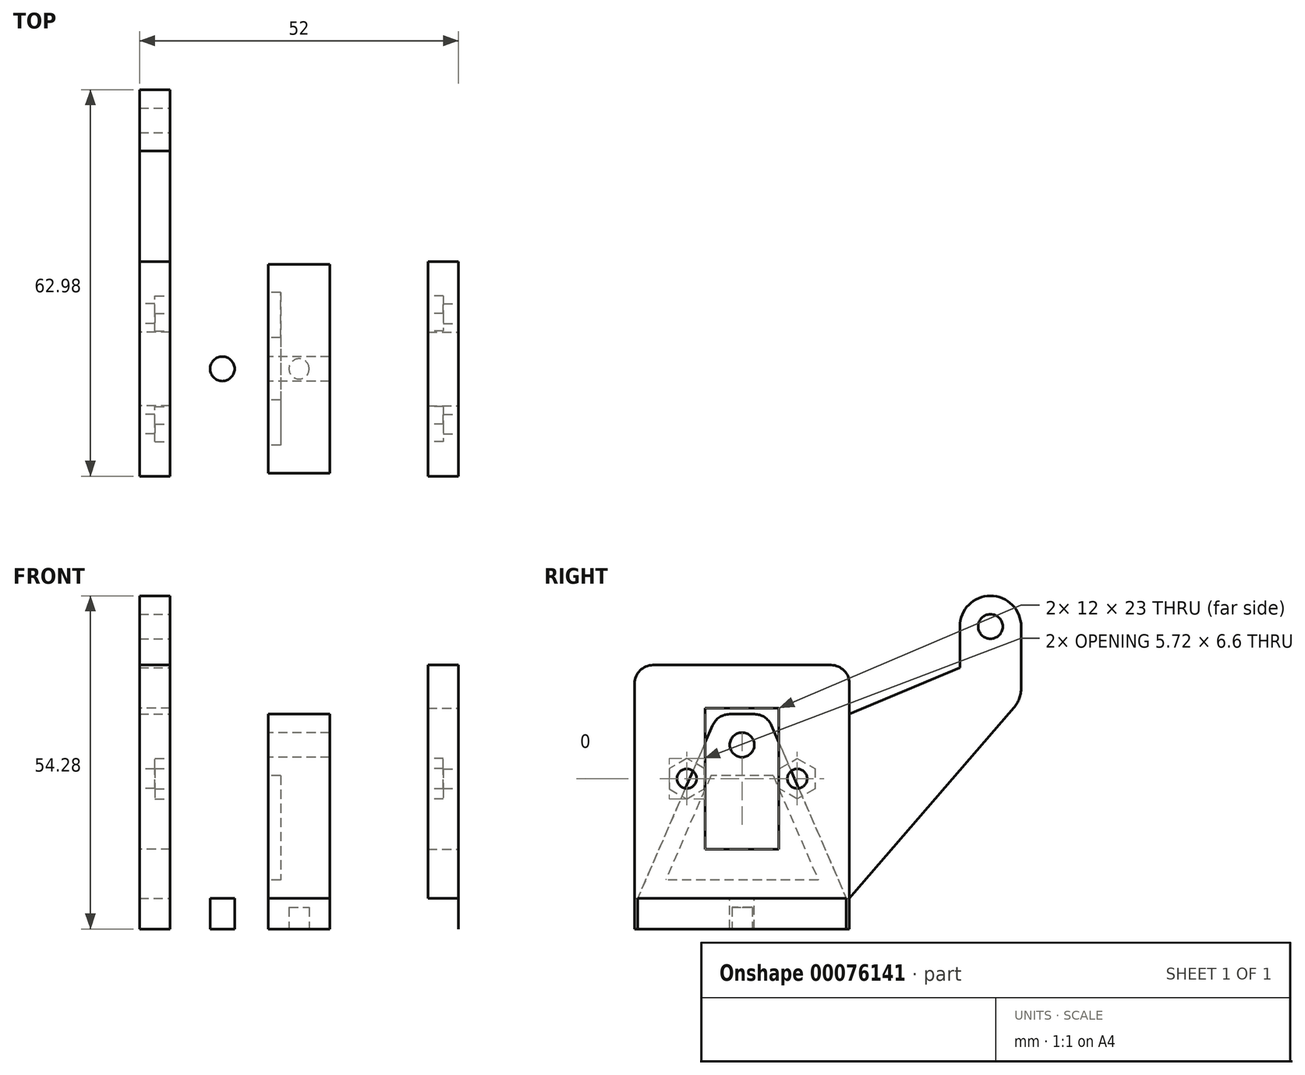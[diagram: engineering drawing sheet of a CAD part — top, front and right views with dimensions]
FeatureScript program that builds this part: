
annotation { "Feature Type Name" : "Feature", "Feature Type Description" : "" }
export const myFeature = defineFeature(function(context is Context, id is Id, definition is map)
    precondition{}
    {
        {
            var Q0;
            Q0=qCreatedBy(makeId("Top.planeOp"),FACE);
            var sketch = newSketch(context, id + "F0", { "sketchPlane" : qUnion([Q0])});
            skLineSegment(sketch, "E0.bottom", {"start": v(-23, 20) * mm, "end": v(23, 20) * mm});
            skLineSegment(sketch, "E0.top", {"start": v(-23, -20) * mm, "end": v(23, -20) * mm});
            skLineSegment(sketch, "E0.left", {"start": v(-26, 17) * mm, "end": v(-26, -17) * mm});
            skLineSegment(sketch, "E0.right", {"start": v(26, 17) * mm, "end": v(26, -17) * mm});
            skPoint(sketch, "E0.middle", {"position": v(0, 0) * mm});
            skPoint(sketch, "E1.visualSharp", {"position": v(-26, 20) * mm});
            skArc(sketch, "E1.filletArc", {"start": v(-23, 20) * mm, "mid": v(-25.12, 19.12) * mm, "end": v(-26, 17) * mm});
            skPoint(sketch, "E2.visualSharp", {"position": v(-26, -20) * mm});
            skArc(sketch, "E2.filletArc", {"start": v(-26, -17) * mm, "mid": v(-25.12, -19.12) * mm, "end": v(-23, -20) * mm});
            skPoint(sketch, "E3.visualSharp", {"position": v(26, -20) * mm});
            skArc(sketch, "E3.filletArc", {"start": v(23, -20) * mm, "mid": v(25.12, -19.12) * mm, "end": v(26, -17) * mm});
            skPoint(sketch, "E4.visualSharp", {"position": v(26, 20) * mm});
            skArc(sketch, "E4.filletArc", {"start": v(26, 17) * mm, "mid": v(25.12, 19.12) * mm, "end": v(23, 20) * mm});
            skSolve(sketch);
        }
        {
            var Q0;
            Q0 = qSketchRegion(id + "F0", true);
            extrude(context, id + "F1", {"entities" : qUnion([Q0]), "depth" : 5 * mm});
        }
        {
            var Q0;
            Q0=makeQuery(id+"F1.opExtrude","CAP_FACE",FACE,{"disambiguationData":[OSD([sQuery(id+"F0.wireOp",EDGE,"E0.bottom"),sQuery(id+"F0.wireOp",EDGE,"E0.top"),sQuery(id+"F0.wireOp",EDGE,"E0.left"),sQuery(id+"F0.wireOp",EDGE,"E0.right"),sQuery(id+"F0.wireOp",EDGE,"E1.filletArc"),sQuery(id+"F0.wireOp",EDGE,"E2.filletArc"),sQuery(id+"F0.wireOp",EDGE,"E3.filletArc"),sQuery(id+"F0.wireOp",EDGE,"E4.filletArc")])],"isStart":true});
            var sketch = newSketch(context, id + "F2", { "sketchPlane" : qUnion([Q0])});
            skCircle(sketch, "E5", {"center": v(0, 0) * mm, "radius": 1.65 * mm});
            skSolve(sketch);
        }
        {
            var Q0;
            Q0 = qSketchRegion(id + "F2", true);
            extrude(context, id + "F3", {"entities" : qUnion([Q0]), "operationType" : NewBodyOperationType.REMOVE, "oppositeDirection" : true, "depth" : 3.5 * mm});
        }
        {
            var Q0;
            Q0=qCreatedBy(makeId("Right.planeOp"),FACE);
            var sketch = newSketch(context, id + "F4", { "sketchPlane" : qUnion([Q0])});
            skLineSegment(sketch, "E6.0", {"start": v(17, 5) * mm, "end": v(-17, 5) * mm});
            skLineSegment(sketch, "E7", {"start": v(0, 5) * mm, "end": v(0, 35) * mm});
            skPoint(sketch, "E7.endSnap0", {"position": v(0, 5) * mm});
            skLineSegment(sketch, "E8", {"start": v(2.03, 35) * mm, "end": v(-2.03, 35) * mm});
            skLineSegment(sketch, "E9", {"start": v(4.78, 33.2) * mm, "end": v(17, 5) * mm});
            skLineSegment(sketch, "E10", {"start": v(-4.78, 33.2) * mm, "end": v(-17, 5) * mm});
            skPoint(sketch, "E11.visualSharp", {"position": v(4, 35) * mm});
            skArc(sketch, "E11.filletArc", {"start": v(4.78, 33.2) * mm, "mid": v(3.68, 34.5) * mm, "end": v(2.03, 35) * mm});
            skPoint(sketch, "E12.visualSharp", {"position": v(-4, 35) * mm});
            skArc(sketch, "E12.filletArc", {"start": v(-2.03, 35) * mm, "mid": v(-3.68, 34.5) * mm, "end": v(-4.78, 33.2) * mm});
            skSolve(sketch);
        }
        {
            var Q0;
            Q0 = qSketchRegion(id + "F4", true);
            extrude(context, id + "F5", {"entities" : qUnion([Q0]), "operationType" : NewBodyOperationType.ADD, "depth" : 5 * mm, "hasSecondDirection" : true, "secondDirectionOppositeDirection" : true, "secondDirectionDepth" : 5 * mm});
        }
        {
            var Q0;
            Q0=makeQuery(id+"F1.opExtrude","SWEPT_FACE",FACE,{"disambiguationData":[OSD([sQuery(id+"F0.wireOp",EDGE,"E0.right")])]});
            var sketch = newSketch(context, id + "F6", { "sketchPlane" : qUnion([Q0])});
            skLineSegment(sketch, "E13.bottom", {"start": v(17.5, 0) * mm, "end": v(-17.5, 0) * mm});
            skLineSegment(sketch, "E13.top", {"start": v(14.5, 43) * mm, "end": v(-14.5, 43) * mm});
            skLineSegment(sketch, "E13.left", {"start": v(17.5, 0) * mm, "end": v(17.5, 40) * mm});
            skLineSegment(sketch, "E13.right", {"start": v(-17.5, 0) * mm, "end": v(-17.5, 40) * mm});
            skLineSegment(sketch, "E14", {"start": v(0, 0) * mm, "end": v(0, 49) * mm, "construction": true});
            skPoint(sketch, "E15.visualSharp", {"position": v(17.5, 43) * mm});
            skArc(sketch, "E15.filletArc", {"start": v(17.5, 40) * mm, "mid": v(16.62, 42.12) * mm, "end": v(14.5, 43) * mm});
            skPoint(sketch, "E16.visualSharp", {"position": v(-17.5, 43) * mm});
            skArc(sketch, "E16.filletArc", {"start": v(-14.5, 43) * mm, "mid": v(-16.62, 42.12) * mm, "end": v(-17.5, 40) * mm});
            skLineSegment(sketch, "E17.bottom", {"start": v(6, 36) * mm, "end": v(-6, 36) * mm});
            skLineSegment(sketch, "E17.top", {"start": v(6, 13) * mm, "end": v(-6, 13) * mm});
            skLineSegment(sketch, "E17.left", {"start": v(6, 36) * mm, "end": v(6, 13) * mm});
            skLineSegment(sketch, "E17.right", {"start": v(-6, 36) * mm, "end": v(-6, 13) * mm});
            skPoint(sketch, "E17.middle", {"position": v(0, 24.5) * mm});
            skLineSegment(sketch, "E18", {"start": v(-17.5, 24.5) * mm, "end": v(17.5, 24.5) * mm, "construction": true});
            skCircle(sketch, "E19", {"center": v(-9, 24.5) * mm, "radius": 1.6 * mm});
            skCircle(sketch, "E20.MirrorC", {"center": v(9, 24.5) * mm, "radius": 1.6 * mm});
            skSolve(sketch);
        }
        {
            var Q0;
            Q0=makeQuery(id+"F6.imprint","IMPRINT",FACE,{"disambiguationData":[TD([[makeQuery(id+"F6.imprint","IMPRINT",EDGE,{"derivedFrom":sQuery(id+"F6.wireOp",EDGE,"E13.top")}),1.0]])]});
            extrude(context, id + "F7", {"entities" : qUnion([Q0]), "oppositeDirection" : true, "depth" : 5 * mm});
        }
        {
            var Q0;
            Q0=makeQuery(id+"F7.opExtrude","CAP_FACE",FACE,{"disambiguationData":[OSD([sQuery(id+"F0.wireOp",EDGE,"E0.right"),sQuery(id+"F0.wireOp",EDGE,"E3.filletArc"),sQuery(id+"F0.wireOp",EDGE,"E4.filletArc"),sQuery(id+"F6.wireOp",EDGE,"E13.bottom"),sQuery(id+"F6.wireOp",EDGE,"E13.top"),sQuery(id+"F6.wireOp",EDGE,"E13.left"),sQuery(id+"F6.wireOp",EDGE,"E13.right"),sQuery(id+"F6.wireOp",EDGE,"E15.filletArc"),sQuery(id+"F6.wireOp",EDGE,"E16.filletArc"),sQuery(id+"F6.wireOp",EDGE,"E17.bottom"),sQuery(id+"F6.wireOp",EDGE,"E17.top"),sQuery(id+"F6.wireOp",EDGE,"E17.left"),sQuery(id+"F6.wireOp",EDGE,"E17.right"),sQuery(id+"F6.wireOp",EDGE,"E19"),sQuery(id+"F6.wireOp",EDGE,"E20.MirrorC")])],"isStart":false});
            var sketch = newSketch(context, id + "F8", { "sketchPlane" : qUnion([Q0])});
            skLineSegment(sketch, "E21", {"start": v(0, 5) * mm, "end": v(0, 43) * mm, "construction": true});
            skCircle(sketch, "E22.cCircle", {"center": v(9, 24.5) * mm, "radius": 2.86 * mm, "construction": true});
            skLineSegment(sketch, "E22.0", {"start": v(9, 27.8) * mm, "end": v(11.86, 26.15) * mm});
            skLineSegment(sketch, "E22.1", {"start": v(11.86, 26.15) * mm, "end": v(11.86, 22.85) * mm});
            skLineSegment(sketch, "E22.2", {"start": v(11.86, 22.85) * mm, "end": v(9, 21.2) * mm});
            skLineSegment(sketch, "E22.3", {"start": v(9, 21.2) * mm, "end": v(6.14, 22.85) * mm});
            skLineSegment(sketch, "E22.4", {"start": v(6.14, 22.85) * mm, "end": v(6.14, 26.15) * mm});
            skLineSegment(sketch, "E22.5", {"start": v(6.14, 26.15) * mm, "end": v(9, 27.8) * mm});
            skPoint(sketch, "E22.0.midPoint", {"position": v(10.43, 26.98) * mm});
            skLineSegment(sketch, "E23.MirrorCS", {"start": v(-9, 21.2) * mm, "end": v(-6.14, 22.85) * mm});
            skLineSegment(sketch, "E24.MirrorCS", {"start": v(-6.14, 22.85) * mm, "end": v(-6.14, 26.15) * mm});
            skCircle(sketch, "E25.MirrorC", {"center": v(-9, 24.5) * mm, "radius": 2.86 * mm, "construction": true});
            skLineSegment(sketch, "E26.MirrorCS", {"start": v(-6.14, 26.15) * mm, "end": v(-9, 27.8) * mm});
            skLineSegment(sketch, "E27.MirrorCS", {"start": v(-9, 27.8) * mm, "end": v(-11.86, 26.15) * mm});
            skLineSegment(sketch, "E28.MirrorCS", {"start": v(-11.86, 22.85) * mm, "end": v(-9, 21.2) * mm});
            skLineSegment(sketch, "E29.MirrorCS", {"start": v(-11.86, 26.15) * mm, "end": v(-11.86, 22.85) * mm});
            skSolve(sketch);
        }
        {
            var Q0;
            Q0 = qSketchRegion(id + "F8", true);
            extrude(context, id + "F9", {"entities" : qUnion([Q0]), "operationType" : NewBodyOperationType.REMOVE, "oppositeDirection" : true, "depth" : 2.5 * mm});
        }
        {
            var Q0;
            Q0=makeQuery(id+"F7.opExtrude","SWEPT_BODY",BODY,{"disambiguationData":[OSD([sQuery(id+"F0.wireOp",EDGE,"E0.right"),sQuery(id+"F0.wireOp",EDGE,"E3.filletArc"),sQuery(id+"F0.wireOp",EDGE,"E4.filletArc"),sQuery(id+"F6.wireOp",EDGE,"E13.bottom"),sQuery(id+"F6.wireOp",EDGE,"E13.top"),sQuery(id+"F6.wireOp",EDGE,"E13.left"),sQuery(id+"F6.wireOp",EDGE,"E13.right"),sQuery(id+"F6.wireOp",EDGE,"E15.filletArc"),sQuery(id+"F6.wireOp",EDGE,"E16.filletArc")])]});
            transform(context, id + "F10", {"entities" : qUnion([Q0]), "transformType" : TransformType.TRANSLATION_3D, "dx" : -47 * mm, "dy" : 0 * mm, "dz" : 0 * mm, "makeCopy" : true});
        }
        {
            var Q0;
            Q0=makeQuery(id+"F10.opPattern","COPY",FACE,{"derivedFrom":makeQuery(id+"F7.opExtrude","CAP_FACE",FACE,{"disambiguationData":[OSD([sQuery(id+"F0.wireOp",EDGE,"E0.right"),sQuery(id+"F0.wireOp",EDGE,"E3.filletArc"),sQuery(id+"F0.wireOp",EDGE,"E4.filletArc"),sQuery(id+"F6.wireOp",EDGE,"E13.bottom"),sQuery(id+"F6.wireOp",EDGE,"E13.top"),sQuery(id+"F6.wireOp",EDGE,"E13.left"),sQuery(id+"F6.wireOp",EDGE,"E13.right"),sQuery(id+"F6.wireOp",EDGE,"E15.filletArc"),sQuery(id+"F6.wireOp",EDGE,"E16.filletArc"),sQuery(id+"F6.wireOp",EDGE,"E17.bottom"),sQuery(id+"F6.wireOp",EDGE,"E17.top"),sQuery(id+"F6.wireOp",EDGE,"E17.left"),sQuery(id+"F6.wireOp",EDGE,"E17.right"),sQuery(id+"F6.wireOp",EDGE,"E19"),sQuery(id+"F6.wireOp",EDGE,"E20.MirrorC")])],"isStart":false}),"instanceName":"1"});
            var Q1;
            Q1=makeQuery(id+"F10.opPattern","COPY",FACE,{"derivedFrom":makeQuery(id+"F7.opExtrude","CAP_FACE",FACE,{"disambiguationData":[OSD([sQuery(id+"F0.wireOp",EDGE,"E0.right"),sQuery(id+"F0.wireOp",EDGE,"E3.filletArc"),sQuery(id+"F0.wireOp",EDGE,"E4.filletArc"),sQuery(id+"F6.wireOp",EDGE,"E13.bottom"),sQuery(id+"F6.wireOp",EDGE,"E13.top"),sQuery(id+"F6.wireOp",EDGE,"E13.left"),sQuery(id+"F6.wireOp",EDGE,"E13.right"),sQuery(id+"F6.wireOp",EDGE,"E15.filletArc"),sQuery(id+"F6.wireOp",EDGE,"E16.filletArc"),sQuery(id+"F6.wireOp",EDGE,"E17.bottom"),sQuery(id+"F6.wireOp",EDGE,"E17.top"),sQuery(id+"F6.wireOp",EDGE,"E17.left"),sQuery(id+"F6.wireOp",EDGE,"E17.right"),sQuery(id+"F6.wireOp",EDGE,"E19"),sQuery(id+"F6.wireOp",EDGE,"E20.MirrorC")])],"isStart":true}),"instanceName":"1"});
            cPlane(context, id + "F11", {"entities" : qUnion([Q0, Q1]), "cplaneType" : CPlaneType.MID_PLANE, "offset" : 150 * mm, "width" : 150 * mm, "height" : 150 * mm});
        }
        {
            var Q0;
            Q0=qCreatedBy(id+"F11.planeOp",FACE);
            var sketch = newSketch(context, id + "F12", { "sketchPlane" : qUnion([Q0])});
            skLineSegment(sketch, "E30", {"start": v(0, 0) * mm, "end": v(0, 42.9) * mm, "construction": true});
            skSolve(sketch);
        }
        {
            var Q0;
            Q0=makeQuery(id+"F10.opPattern","COPY",BODY,{"derivedFrom":makeQuery(id+"F7.opExtrude","SWEPT_BODY",BODY,{"disambiguationData":[OSD([sQuery(id+"F0.wireOp",EDGE,"E0.right"),sQuery(id+"F0.wireOp",EDGE,"E3.filletArc"),sQuery(id+"F0.wireOp",EDGE,"E4.filletArc"),sQuery(id+"F6.wireOp",EDGE,"E13.bottom"),sQuery(id+"F6.wireOp",EDGE,"E13.top"),sQuery(id+"F6.wireOp",EDGE,"E13.left"),sQuery(id+"F6.wireOp",EDGE,"E13.right"),sQuery(id+"F6.wireOp",EDGE,"E15.filletArc"),sQuery(id+"F6.wireOp",EDGE,"E16.filletArc"),sQuery(id+"F6.wireOp",EDGE,"E17.bottom"),sQuery(id+"F6.wireOp",EDGE,"E17.top"),sQuery(id+"F6.wireOp",EDGE,"E17.left"),sQuery(id+"F6.wireOp",EDGE,"E17.right"),sQuery(id+"F6.wireOp",EDGE,"E19"),sQuery(id+"F6.wireOp",EDGE,"E20.MirrorC")])]}),"instanceName":"1"});
            var Q1;
            Q1=sQuery(id+"F12.wireOp",EDGE,"E30");
            transform(context, id + "F13", {"entities" : qUnion([Q0]), "transformType" : TransformType.ROTATION, "transformAxis" : qUnion([Q1]), "angle" : 180 * degree, "makeCopy" : false});
        }
        {
            var Q0;
            Q0=makeQuery(id+"F5.opExtrude","CAP_FACE",FACE,{"disambiguationData":[OSD([sQuery(id+"F4.wireOp",EDGE,"E6.0"),sQuery(id+"F4.wireOp",EDGE,"E8"),sQuery(id+"F4.wireOp",EDGE,"E9"),sQuery(id+"F4.wireOp",EDGE,"E10"),sQuery(id+"F4.wireOp",EDGE,"E11.filletArc"),sQuery(id+"F4.wireOp",EDGE,"E12.filletArc")])],"isStart":true});
            var sketch = newSketch(context, id + "F14", { "sketchPlane" : qUnion([Q0])});
            skCircle(sketch, "E31", {"center": v(0, 30) * mm, "radius": 2 * mm});
            skSolve(sketch);
        }
        {
            var Q0;
            Q0=makeQuery(id+"F14.imprint","IMPRINT",FACE,{"disambiguationData":[TD([[makeQuery(id+"F14.imprint","IMPRINT",EDGE,{"derivedFrom":sQuery(id+"F14.wireOp",EDGE,"E31")}),1.0]])]});
            extrude(context, id + "F15", {"entities" : qUnion([Q0]), "operationType" : NewBodyOperationType.REMOVE, "oppositeDirection" : true, "depth" : 25 * mm});
        }
        {
            var Q0;
            Q0=makeQuery(id+"F10.opPattern","COPY",FACE,{"derivedFrom":makeQuery(id+"F7.opExtrude","CAP_FACE",FACE,{"disambiguationData":[OSD([sQuery(id+"F0.wireOp",EDGE,"E0.right"),sQuery(id+"F0.wireOp",EDGE,"E3.filletArc"),sQuery(id+"F0.wireOp",EDGE,"E4.filletArc"),sQuery(id+"F6.wireOp",EDGE,"E13.bottom"),sQuery(id+"F6.wireOp",EDGE,"E13.top"),sQuery(id+"F6.wireOp",EDGE,"E13.left"),sQuery(id+"F6.wireOp",EDGE,"E13.right"),sQuery(id+"F6.wireOp",EDGE,"E15.filletArc"),sQuery(id+"F6.wireOp",EDGE,"E16.filletArc"),sQuery(id+"F6.wireOp",EDGE,"E17.bottom"),sQuery(id+"F6.wireOp",EDGE,"E17.top"),sQuery(id+"F6.wireOp",EDGE,"E17.left"),sQuery(id+"F6.wireOp",EDGE,"E17.right"),sQuery(id+"F6.wireOp",EDGE,"E19"),sQuery(id+"F6.wireOp",EDGE,"E20.MirrorC")])],"isStart":false}),"instanceName":"1"});
            var sketch = newSketch(context, id + "F16", { "sketchPlane" : qUnion([Q0])});
            skLineSegment(sketch, "E32.0", {"start": v(17.5, 0) * mm, "end": v(17.5, 5) * mm});
            skLineSegment(sketch, "E33", {"start": v(17.5, 5) * mm, "end": v(17.5, 35) * mm});
            skLineSegment(sketch, "E34", {"start": v(17.5, 35) * mm, "end": v(17.5, 40) * mm});
            skPoint(sketch, "E35", {"position": v(17.5, 20) * mm});
            skLineSegment(sketch, "E36", {"start": v(17.5, 20) * mm, "end": v(40.48, 39.28) * mm, "construction": true});
            skLineSegment(sketch, "E37", {"start": v(44.27, 36.02) * mm, "end": v(17.5, 5) * mm});
            skLineSegment(sketch, "E38", {"start": v(38.54, 43.89) * mm, "end": v(17.5, 35) * mm});
            skLineSegment(sketch, "E39", {"start": v(40.48, 39.28) * mm, "end": v(40.48, 49.28) * mm, "construction": true});
            skLineSegment(sketch, "E40", {"start": v(35.48, 49.28) * mm, "end": v(35.48, 39.28) * mm});
            skLineSegment(sketch, "E41", {"start": v(45.48, 49.28) * mm, "end": v(45.48, 49.28) * mm});
            skLineSegment(sketch, "E42", {"start": v(45.48, 39.28) * mm, "end": v(45.48, 39.28) * mm});
            skLineSegment(sketch, "E43", {"start": v(35.48, 39.28) * mm, "end": v(35.48, 39.28) * mm});
            skArc(sketch, "E44", {"start": v(45.48, 39.28) * mm, "mid": v(40.48, 44.28) * mm, "end": v(35.48, 39.28) * mm, "construction": true});
            skLineSegment(sketch, "E45", {"start": v(45.48, 49.28) * mm, "end": v(45.48, 39.28) * mm});
            skArc(sketch, "E46", {"start": v(35.48, 49.28) * mm, "mid": v(40.48, 44.28) * mm, "end": v(45.48, 49.28) * mm, "construction": true});
            skArc(sketch, "E47", {"start": v(45.48, 49.28) * mm, "mid": v(40.48, 54.28) * mm, "end": v(35.48, 49.28) * mm});
            skArc(sketch, "E48", {"start": v(44.27, 36.02) * mm, "mid": v(45.17, 37.54) * mm, "end": v(45.48, 39.28) * mm});
            skArc(sketch, "E49", {"start": v(35.48, 39.28) * mm, "mid": v(38.74, 34.6) * mm, "end": v(44.27, 36.02) * mm, "construction": true});
            skSolve(sketch);
        }
        {
            var Q0;
            Q0 = qSketchRegion(id + "F16", true);
            extrude(context, id + "F17", {"entities" : qUnion([Q0]), "operationType" : NewBodyOperationType.ADD, "oppositeDirection" : true, "depth" : (5) * mm});
        }
        {
            var Q0;
            Q0=makeQuery(id+"F17.boolean.opBoolean","MERGE",FACE,{"derivedFrom":[makeQuery(id+"F10.opPattern","COPY",FACE,{"derivedFrom":makeQuery(id+"F7.opExtrude","CAP_FACE",FACE,{"disambiguationData":[OSD([sQuery(id+"F0.wireOp",EDGE,"E0.right"),sQuery(id+"F0.wireOp",EDGE,"E3.filletArc"),sQuery(id+"F0.wireOp",EDGE,"E4.filletArc"),sQuery(id+"F6.wireOp",EDGE,"E13.bottom"),sQuery(id+"F6.wireOp",EDGE,"E13.top"),sQuery(id+"F6.wireOp",EDGE,"E13.left"),sQuery(id+"F6.wireOp",EDGE,"E13.right"),sQuery(id+"F6.wireOp",EDGE,"E15.filletArc"),sQuery(id+"F6.wireOp",EDGE,"E16.filletArc"),sQuery(id+"F6.wireOp",EDGE,"E17.bottom"),sQuery(id+"F6.wireOp",EDGE,"E17.top"),sQuery(id+"F6.wireOp",EDGE,"E17.left"),sQuery(id+"F6.wireOp",EDGE,"E17.right"),sQuery(id+"F6.wireOp",EDGE,"E19"),sQuery(id+"F6.wireOp",EDGE,"E20.MirrorC")])],"isStart":false}),"instanceName":"1"}),makeQuery(id+"F17.opExtrude","CAP_FACE",FACE,{"disambiguationData":[OSD([sQuery(id+"F16.wireOp",EDGE,"E33"),sQuery(id+"F16.wireOp",EDGE,"E37"),sQuery(id+"F16.wireOp",EDGE,"E38"),sQuery(id+"F16.wireOp",EDGE,"E40"),sQuery(id+"F16.wireOp",EDGE,"E45"),sQuery(id+"F16.wireOp",EDGE,"E47"),sQuery(id+"F16.wireOp",EDGE,"E48")])],"isStart":true})]});
            var sketch = newSketch(context, id + "F18", { "sketchPlane" : qUnion([Q0])});
            skCircle(sketch, "E50", {"center": v(40.48, 49.28) * mm, "radius": 2 * mm});
            skSolve(sketch);
        }
        {
            var Q0;
            Q0=makeQuery(id+"F18.imprint","IMPRINT",FACE,{"disambiguationData":[TD([[makeQuery(id+"F18.imprint","IMPRINT",EDGE,{"derivedFrom":sQuery(id+"F18.wireOp",EDGE,"E50")}),1.0]])]});
            extrude(context, id + "F19", {"entities" : qUnion([Q0]), "operationType" : NewBodyOperationType.REMOVE, "endBound" : BoundingType.THROUGH_ALL, "oppositeDirection" : true, "depth" : 25 * mm});
        }
        {
            var Q0;
            Q0=makeQuery(id+"F1.opExtrude","CAP_FACE",FACE,{"disambiguationData":[OSD([sQuery(id+"F0.wireOp",EDGE,"E0.bottom"),sQuery(id+"F0.wireOp",EDGE,"E0.top"),sQuery(id+"F0.wireOp",EDGE,"E0.left"),sQuery(id+"F0.wireOp",EDGE,"E0.right"),sQuery(id+"F0.wireOp",EDGE,"E1.filletArc"),sQuery(id+"F0.wireOp",EDGE,"E2.filletArc"),sQuery(id+"F0.wireOp",EDGE,"E3.filletArc"),sQuery(id+"F0.wireOp",EDGE,"E4.filletArc")])],"isStart":false});
            var sketch = newSketch(context, id + "F20", { "sketchPlane" : qUnion([Q0])});
            skCircle(sketch, "E51", {"center": v(12.5, 0) * mm, "radius": 2 * mm});
            skCircle(sketch, "E52.MirrorC", {"center": v(-12.5, 0) * mm, "radius": 2 * mm});
            skSolve(sketch);
        }
        {
            var Q0;
            Q0=makeQuery(id+"F20.imprint","IMPRINT",FACE,{"disambiguationData":[TD([[makeQuery(id+"F20.imprint","IMPRINT",EDGE,{"derivedFrom":sQuery(id+"F20.wireOp",EDGE,"E52.MirrorC")}),-1.0]])]});
            var Q1;
            Q1=makeQuery(id+"F20.imprint","IMPRINT",FACE,{"disambiguationData":[TD([[makeQuery(id+"F20.imprint","IMPRINT",EDGE,{"derivedFrom":sQuery(id+"F20.wireOp",EDGE,"E51")}),1.0]])]});
            extrude(context, id + "F21", {"entities" : qUnion([Q0, Q1]), "operationType" : NewBodyOperationType.REMOVE, "endBound" : BoundingType.THROUGH_ALL, "oppositeDirection" : true, "depth" : 25 * mm});
        }
        {
            var Q0;
            Q0=makeQuery(id+"F5.opExtrude","CAP_FACE",FACE,{"disambiguationData":[OSD([sQuery(id+"F4.wireOp",EDGE,"E6.0"),sQuery(id+"F4.wireOp",EDGE,"E8"),sQuery(id+"F4.wireOp",EDGE,"E9"),sQuery(id+"F4.wireOp",EDGE,"E10"),sQuery(id+"F4.wireOp",EDGE,"E11.filletArc"),sQuery(id+"F4.wireOp",EDGE,"E12.filletArc")])],"isStart":true});
            var sketch = newSketch(context, id + "F22", { "sketchPlane" : qUnion([Q0])});
            skLineSegment(sketch, "E53.1", {"start": v(-12.43, 8) * mm, "end": v(12.43, 8) * mm});
            skLineSegment(sketch, "E54", {"start": v(-5.06, 25) * mm, "end": v(5.06, 25) * mm});
            skLineSegment(sketch, "E55", {"start": v(5.06, 25) * mm, "end": v(12.43, 8) * mm});
            skLineSegment(sketch, "E56", {"start": v(-5.06, 25) * mm, "end": v(-12.43, 8) * mm});
            skSolve(sketch);
        }
        {
            var Q0;
            Q0=makeQuery(id+"F22.imprint","IMPRINT",FACE,{"disambiguationData":[TD([[makeQuery(id+"F22.imprint","IMPRINT",EDGE,{"derivedFrom":sQuery(id+"F22.wireOp",EDGE,"E53.1")}),1.0]])]});
            extrude(context, id + "F23", {"entities" : qUnion([Q0]), "operationType" : NewBodyOperationType.REMOVE, "oppositeDirection" : true, "depth" : (2) * mm});
        }
    });
